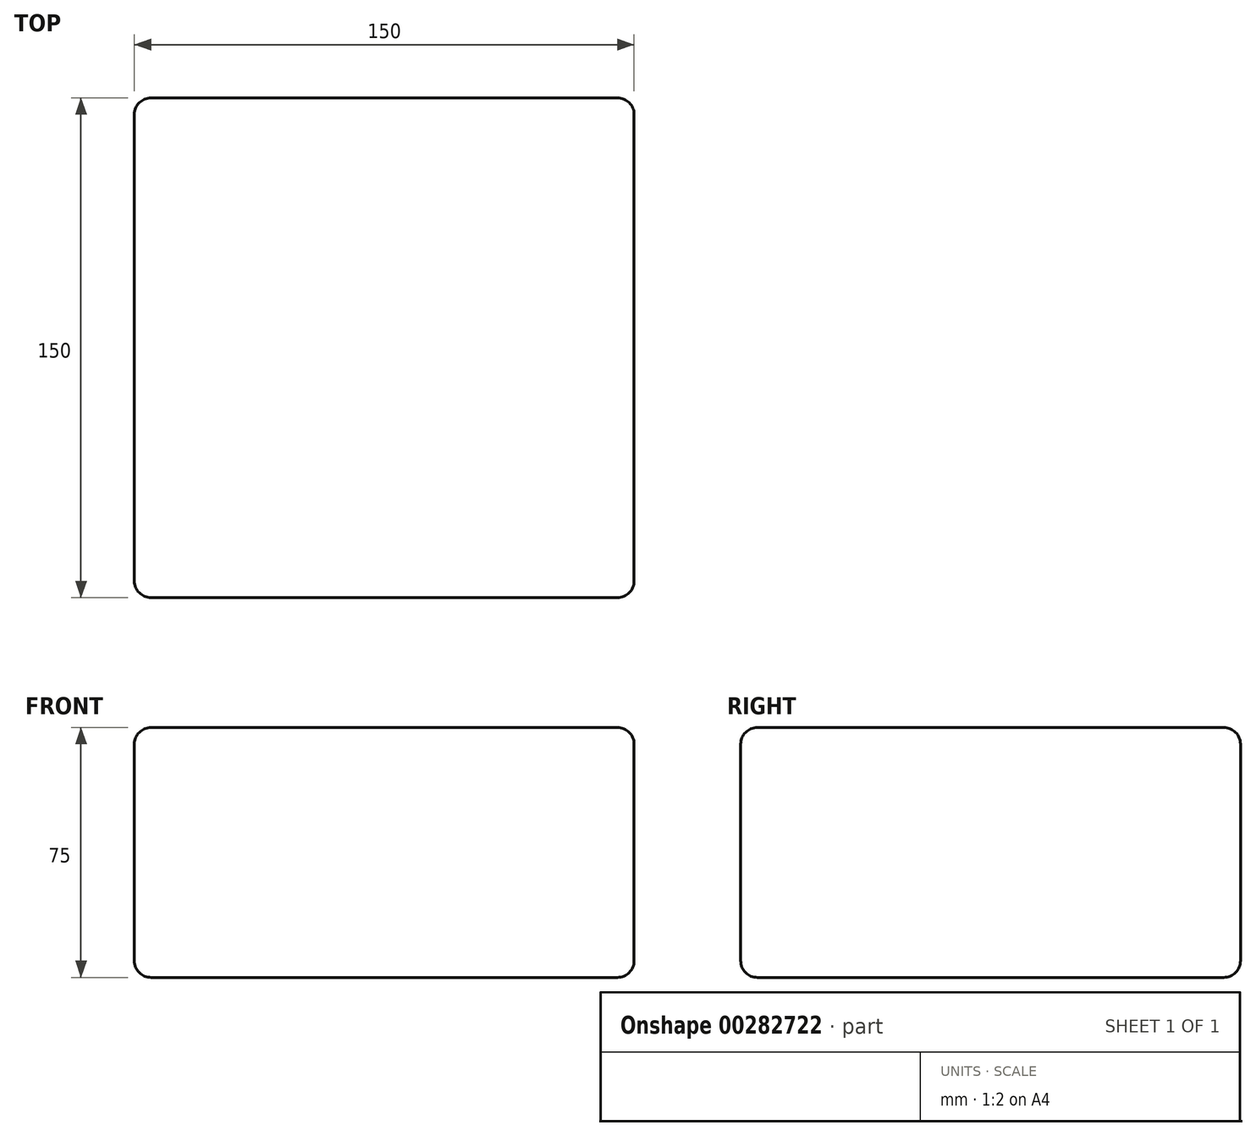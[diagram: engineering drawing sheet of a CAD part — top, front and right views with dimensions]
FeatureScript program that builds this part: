
annotation { "Feature Type Name" : "Feature", "Feature Type Description" : "" }
export const myFeature = defineFeature(function(context is Context, id is Id, definition is map)
    precondition{}
    {
        {
            var Q0;
            Q0=qCreatedBy(makeId("Top.planeOp"),FACE);
            var sketch = newSketch(context, id + "F0", { "sketchPlane" : qUnion([Q0])});
            skLineSegment(sketch, "E0.bottom", {"start": v(-76.2, -74.86) * mm, "end": v(73.8, -74.86) * mm});
            skLineSegment(sketch, "E0.top", {"start": v(-76.2, 75.14) * mm, "end": v(73.8, 75.14) * mm});
            skLineSegment(sketch, "E0.left", {"start": v(-76.2, -74.86) * mm, "end": v(-76.2, 75.14) * mm});
            skLineSegment(sketch, "E0.right", {"start": v(73.8, -74.86) * mm, "end": v(73.8, 75.14) * mm});
            skSolve(sketch);
        }
        {
            var Q0;
            Q0=makeQuery(id+"F0.imprint","IMPRINT",FACE,{"disambiguationData":[TD([[makeQuery(id+"F0.imprint","IMPRINT",EDGE,{"derivedFrom":sQuery(id+"F0.wireOp",EDGE,"E0.bottom")}),1.0]])]});
            extrude(context, id + "F1", {"entities" : qUnion([Q0]), "depth" : 75 * mm});
        }
        {
            var Q0;
            Q0=makeQuery(id+"F1.opExtrude","SWEPT_FACE",FACE,{"disambiguationData":[OSD([sQuery(id+"F0.wireOp",EDGE,"E0.bottom")])]});
            fillet(context, id + "F2", {"entities" : qUnion([Q0]), "radius" : 5 * mm, "tangentPropagation" : true, "allowEdgeOverflow" : false});
        }
        {
            var Q0;
            Q0=makeQuery(id+"F1.opExtrude","SWEPT_FACE",FACE,{"disambiguationData":[OSD([sQuery(id+"F0.wireOp",EDGE,"E0.right")])]});
            var Q1;
            Q1=makeQuery(id+"F1.opExtrude","SWEPT_FACE",FACE,{"disambiguationData":[OSD([sQuery(id+"F0.wireOp",EDGE,"E0.right")])]});
            fillet(context, id + "F3", {"entities" : qUnion([Q0, Q1]), "radius" : 5 * mm, "tangentPropagation" : true, "allowEdgeOverflow" : false});
        }
        {
            var Q0;
            Q0=makeQuery(id+"F1.opExtrude","SWEPT_FACE",FACE,{"disambiguationData":[OSD([sQuery(id+"F0.wireOp",EDGE,"E0.top")])]});
            fillet(context, id + "F4", {"entities" : qUnion([Q0]), "radius" : 5 * mm, "tangentPropagation" : true, "allowEdgeOverflow" : false});
        }
        {
            var Q0;
            Q0=makeQuery(id+"F1.opExtrude","SWEPT_FACE",FACE,{"disambiguationData":[OSD([sQuery(id+"F0.wireOp",EDGE,"E0.left")])]});
            fillet(context, id + "F5", {"entities" : qUnion([Q0]), "radius" : 5 * mm, "tangentPropagation" : true, "allowEdgeOverflow" : false});
        }
    });
